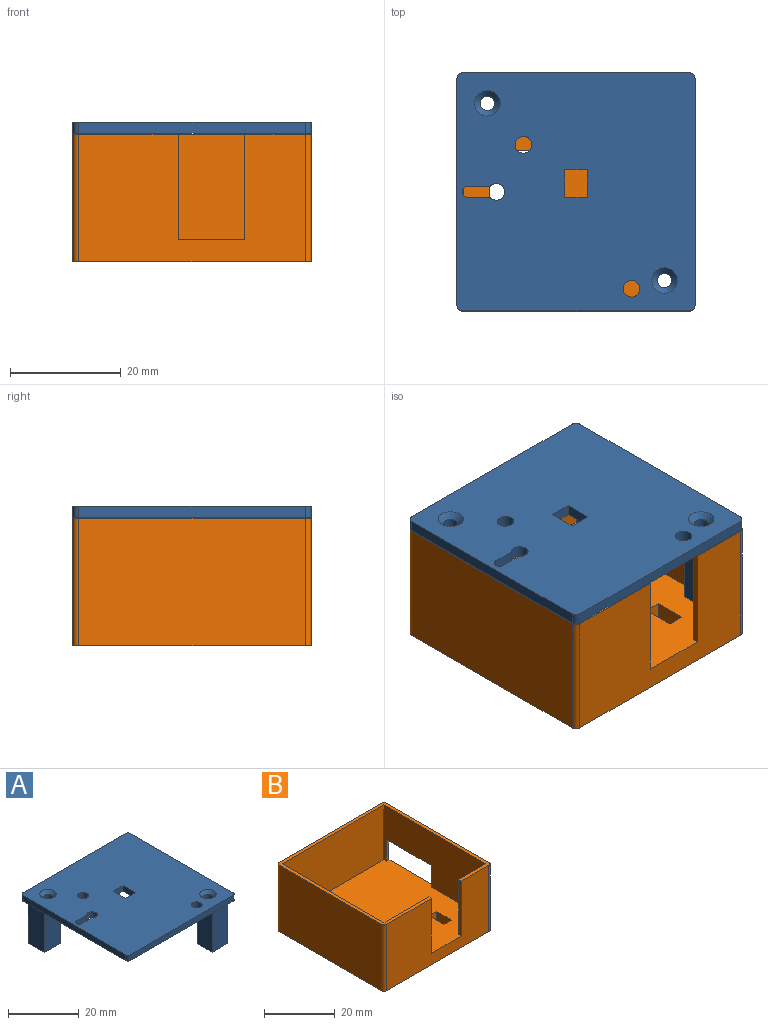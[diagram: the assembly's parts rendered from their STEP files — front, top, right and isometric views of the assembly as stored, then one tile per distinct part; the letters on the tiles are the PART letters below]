
ASSEMBLY  parts=2 mates=1
PART A: 34 faces, bbox 43x43x17 mm
  f0: plane 6.5x6.5mm, normal (0,0,-1), area 36.9mm2, adj f1,f2,f22,f28,f29
  f1: plane 15x6.5mm, normal (1,0,0), area 97.5mm2, adj f0,f2,f10,f28
  f2: plane 15x6.5mm, normal (0,-1,0), area 97.5mm2, adj f0,f1,f10,f29
  f3: plane 15x6mm, normal (-1,0,0), area 90mm2, adj f4,f10,f25,f26
  f4: plane 15x6.3mm, normal (0,1,0), area 94.5mm2, adj f3,f10,f25,f27
  f5: plane 41x2mm, normal (-1,0,0), area 82mm2, adj f9,f10,f30,f33
  f6: plane 41x2mm, normal (0,-1,0), area 82mm2, adj f9,f10,f30,f31
  f7: plane 41x2mm, normal (1,0,0), area 82mm2, adj f9,f10,f31,f32
  f8: plane 41x2mm, normal (0,1,0), area 82mm2, adj f9,f10,f32,f33
  f9: plane 43x43mm, normal (0,0,1), area 1764.7mm2, adj f5,f6,f7,f8,f11,f12,f13,f14
  f10: plane 43x43mm, normal (0,0,-1), area 1717.8mm2, adj f1,f2,f3,f4,f5,f6,f7,f8
  f11: cylinder r=1mm len=2mm, axis (0,0,1), area 6.3mm2, adj f9,f10,f12,f14
  f12: plane 4x2mm, normal (0,1,0), area 8mm2, adj f9,f10,f11,f13
  f13: cylinder r=1.5mm len=3mm, axis (0,0,1), area 14.5mm2, adj f9,f10,f12,f14
  f14: plane 4x2mm, normal (0,-1,0), area 8mm2, adj f9,f10,f11,f13
  f15: cylinder r=1.5mm len=3mm, axis (0,0,1), area 18.8mm2, adj f9,f10
  f16: cylinder r=1.5mm len=3mm, axis (0,0,1), area 18.8mm2, adj f9,f10
  f17: cylinder r=1.3mm len=16mm, axis (0,0,1), area 130.7mm2, adj f23,f25
  f18: plane 5x2mm, normal (-1,0,0), area 10mm2, adj f9,f10,f19,f21
  f19: plane 4x2mm, normal (0,-1,0), area 8mm2, adj f9,f10,f18,f20
  f20: plane 5x2mm, normal (1,0,0), area 10mm2, adj f9,f10,f19,f21
  f21: plane 4x2mm, normal (0,1,0), area 8mm2, adj f9,f10,f18,f20
  f22: cylinder r=1.3mm len=16mm, axis (0,0,1), area 130.7mm2, adj f0,f24
  f23: cone r=1.3mm half-angle=45deg, axis (0,0,1), area 16mm2, adj f9,f17
  f24: cone r=1.3mm half-angle=45deg, axis (0,0,1), area 16mm2, adj f9,f22
  f25: plane 6.3x6mm, normal (0,0,-1), area 32.5mm2, adj f3,f4,f17,f26,f27
  f26: plane 15x6.3mm, normal (0,-1,0), area 94.5mm2, adj f3,f10,f25,f27
  f27: plane 15x6mm, normal (1,0,0), area 90mm2, adj f4,f10,f25,f26
  f28: plane 15x6.5mm, normal (0,1,0), area 97.5mm2, adj f0,f1,f10,f29
  f29: plane 15x6.5mm, normal (-1,0,0), area 97.5mm2, adj f0,f2,f10,f28
  f30: cylinder r=1mm len=2mm, axis (0,0,-1), area 3.1mm2, adj f5,f6,f9,f10
  f31: cylinder r=1mm len=2mm, axis (0,0,1), area 3.1mm2, adj f6,f7,f9,f10
  f32: cylinder r=1mm len=2mm, axis (0,0,-1), area 3.1mm2, adj f7,f8,f9,f10
  f33: cylinder r=1mm len=2mm, axis (0,0,1), area 3.1mm2, adj f5,f8,f9,f10
PART B: 45 faces, bbox 43x43x23 mm
  f0: plane 43x43mm, normal (0,0,-1), area 1673mm2, adj f8,f9,f10,f11,f14,f15,f16,f17
  f1: cylinder r=1.3mm len=2.6mm, axis (0,0,1), area 16.3mm2, adj f7,f33
  f2: cylinder r=1.3mm len=2.6mm, axis (0,0,1), area 16.3mm2, adj f7,f40
  f3: plane 7.5x1.1mm, normal (0,1,0), area 8.3mm2, adj f5,f7,f10,f23
  f4: plane 7.5x1.1mm, normal (0,-1,0), area 8.3mm2, adj f5,f7,f10,f23
  f5: plane 18x1.1mm, normal (0,0,-1), area 19.8mm2, adj f3,f4,f10,f23
  f6: plane 43x43mm, normal (0,0,1), area 170.3mm2, adj f8,f9,f10,f11,f12,f13,f22,f23
  f7: plane 41.9x41.9mm, normal (0,0,1), area 1558.6mm2, adj f1,f2,f3,f4,f9,f10,f12,f13
  f8: plane 41x23mm, normal (-1,0,0), area 943mm2, adj f0,f6,f41,f44
  f9: plane 41x23mm, normal (0,-1,0), area 715mm2, adj f0,f6,f7,f12,f13,f41,f42
  f10: plane 41x23mm, normal (1,0,0), area 808mm2, adj f0,f3,f4,f5,f6,f7,f42,f43
  f11: plane 41x23mm, normal (0,1,0), area 943mm2, adj f0,f6,f43,f44
  f12: plane 19x1.1mm, normal (-1,0,0), area 20.9mm2, adj f6,f7,f9,f25
  f13: plane 19x1.1mm, normal (1,0,0), area 20.9mm2, adj f6,f7,f9,f22
  f14: plane 6x4mm, normal (1,0,0), area 24mm2, adj f0,f7,f15,f17
  f15: plane 4x3mm, normal (0,1,0), area 12mm2, adj f0,f7,f14,f16
  f16: plane 6x4mm, normal (-1,0,0), area 24mm2, adj f0,f7,f15,f17
  f17: plane 4x3mm, normal (0,-1,0), area 12mm2, adj f0,f7,f14,f16
  f18: plane 12x4mm, normal (1,0,0), area 48mm2, adj f0,f7,f19,f21
  f19: plane 9.2x4mm, normal (0,1,0), area 36.8mm2, adj f0,f7,f18,f20
  f20: plane 12x4mm, normal (-1,0,0), area 48mm2, adj f0,f7,f19,f21
  f21: plane 9.2x4mm, normal (0,-1,0), area 36.8mm2, adj f0,f7,f18,f20
  f22: plane 19x17.9mm, normal (0,1,0), area 340.1mm2, adj f6,f7,f13,f24
  f23: plane 40.8x19mm, normal (-1,0,0), area 640.2mm2, adj f3,f4,f5,f6,f7,f25,f26
  f24: plane 40.8x19mm, normal (1,0,0), area 775.2mm2, adj f6,f7,f22,f26
  f25: plane 19x10.9mm, normal (0,1,0), area 207.1mm2, adj f6,f7,f12,f23
  f26: plane 40.8x19mm, normal (0,-1,0), area 775.2mm2, adj f6,f7,f23,f24
  f27: plane 2.6x2mm, normal (-0.87,-0.5,0), area 6mm2, adj f0,f28,f32,f33
  f28: plane 2.6x2mm, normal (-0.87,0.5,0), area 6mm2, adj f0,f27,f29,f33
  f29: plane 3x2mm, normal (0,1,0), area 6mm2, adj f0,f28,f30,f33
  f30: plane 2.6x2mm, normal (0.87,0.5,0), area 6mm2, adj f0,f29,f31,f33
  f31: plane 2.6x2mm, normal (0.87,-0.5,0), area 6mm2, adj f0,f30,f32,f33
  f32: plane 3x2mm, normal (0,-1,0), area 6mm2, adj f0,f27,f31,f33
  f33: plane 6x5.2mm, normal (0,0,-1), area 18.1mm2, adj f1,f27,f28,f29,f30,f31,f32
  f34: plane 2.6x2mm, normal (-0.87,-0.5,0), area 6mm2, adj f0,f35,f39,f40
  f35: plane 2.6x2mm, normal (-0.87,0.5,0), area 6mm2, adj f0,f34,f36,f40
  f36: plane 3x2mm, normal (0,1,0), area 6mm2, adj f0,f35,f37,f40
  f37: plane 2.6x2mm, normal (0.87,0.5,0), area 6mm2, adj f0,f36,f38,f40
  f38: plane 2.6x2mm, normal (0.87,-0.5,0), area 6mm2, adj f0,f37,f39,f40
  f39: plane 3x2mm, normal (0,-1,0), area 6mm2, adj f0,f34,f38,f40
  f40: plane 6x5.2mm, normal (0,0,-1), area 18.1mm2, adj f2,f34,f35,f36,f37,f38,f39
  f41: cylinder r=1mm len=23mm, axis (0,0,-1), area 36.1mm2, adj f0,f6,f8,f9
  f42: cylinder r=1mm len=23mm, axis (0,0,1), area 36.1mm2, adj f0,f6,f9,f10
  f43: cylinder r=1mm len=23mm, axis (0,0,-1), area 36.1mm2, adj f0,f6,f10,f11
  f44: cylinder r=1mm len=23mm, axis (0,0,1), area 36.1mm2, adj f0,f6,f8,f11
PLACE A t=(-51.84,-32.25,34.94)mm
PLACE B t=(24.8,-31.27,11.75)mm
MATE slider A.f17 <-> B.f1  axis (0,0,-1) through (-0.79,-3.87,19.94)mm
